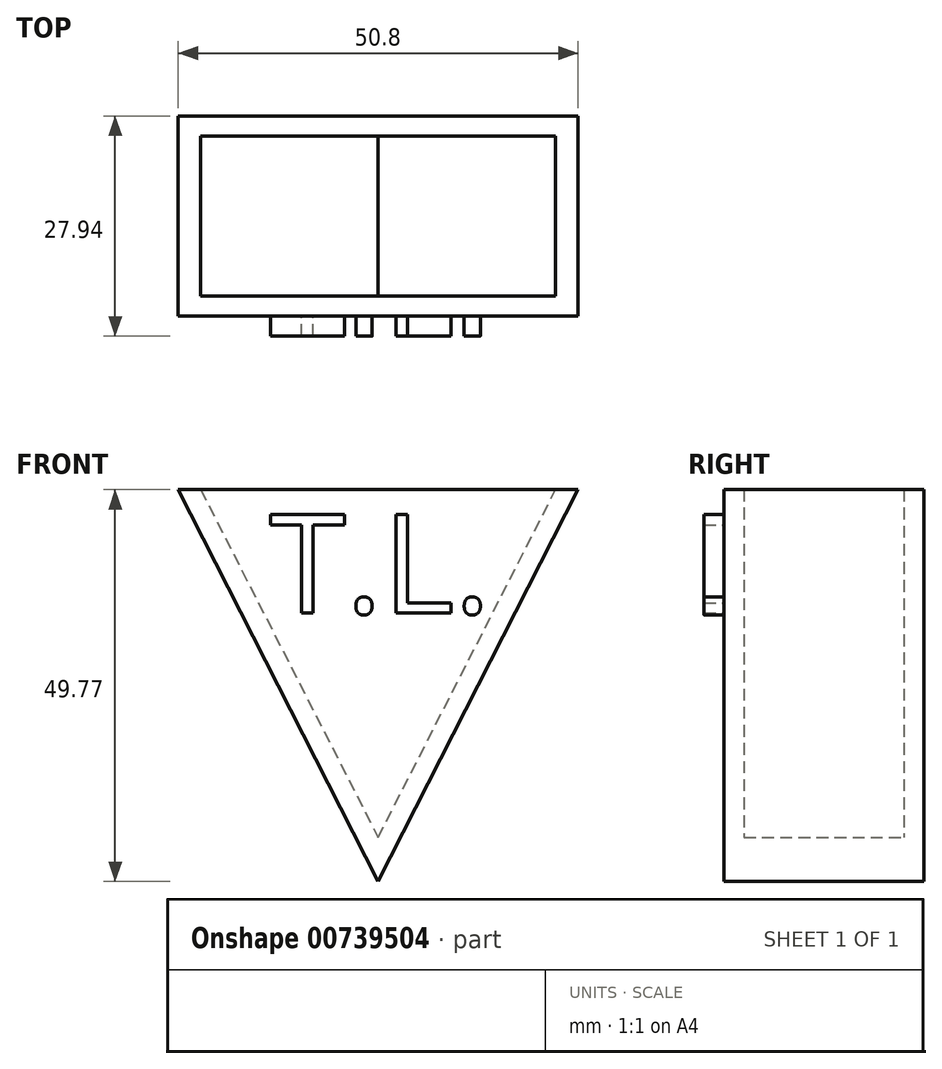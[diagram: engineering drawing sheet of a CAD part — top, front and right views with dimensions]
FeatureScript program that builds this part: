
annotation { "Feature Type Name" : "Feature", "Feature Type Description" : "" }
export const myFeature = defineFeature(function(context is Context, id is Id, definition is map)
    precondition{}
    {
        {
            var Q0;
            Q0=qCreatedBy(makeId("Front.planeOp"),FACE);
            var sketch = newSketch(context, id + "F0", { "sketchPlane" : qUnion([Q0])});
            skLineSegment(sketch, "E0", {"start": v(-25.4, 0) * mm, "end": v(0, -49.77) * mm});
            skLineSegment(sketch, "E1", {"start": v(0, -49.77) * mm, "end": v(25.4, 0) * mm});
            skLineSegment(sketch, "E2", {"start": v(0, 0) * mm, "end": v(25.4, 0) * mm});
            skLineSegment(sketch, "E3", {"start": v(0, 0) * mm, "end": v(-25.4, 0) * mm});
            skLineSegment(sketch, "E4", {"start": v(0, 0) * mm, "end": v(0, -50.8) * mm});
            skSolve(sketch);
        }
        {
            var Q0;
            {var subQ0=sQuery(id+"F0.wireOp",EDGE,"E1");Q0=makeQuery(id+"F0.imprint","IMPRINT",FACE,{"disambiguationData":[TD([[makeQuery(id+"F0.imprint","IMPRINT",EDGE,{"derivedFrom":subQ0}),1.0]])]});}
            var Q1;
            {var subQ0=sQuery(id+"F0.wireOp",EDGE,"E0");Q1=makeQuery(id+"F0.imprint","IMPRINT",FACE,{"disambiguationData":[TD([[makeQuery(id+"F0.imprint","IMPRINT",EDGE,{"derivedFrom":subQ0}),1.0]])]});}
            extrude(context, id + "F1", {"entities" : qUnion([Q0, Q1]), "depth" : 25.4 * mm, "offsetDistance" : 25.4 * mm});
        }
        {
            var Q0;
            Q0=makeQuery(id+"F1.opExtrude","SWEPT_FACE",FACE,{"disambiguationData":[OSD([sQuery(id+"F0.wireOp",EDGE,"E2"),sQuery(id+"F0.wireOp",EDGE,"E3")])]});
            shell(context, id + "F2", {"entities" : qUnion([Q0]), "thickness" : 2.54 * mm});
        }
        {
            var Q0;
            Q0=makeQuery(id+"F1.opExtrude","CAP_FACE",FACE,{"disambiguationData":[OSD([sQuery(id+"F0.wireOp",EDGE,"E0"),sQuery(id+"F0.wireOp",EDGE,"E1"),sQuery(id+"F0.wireOp",EDGE,"E2"),sQuery(id+"F0.wireOp",EDGE,"E3")])],"isStart":false});
            var sketch = newSketch(context, id + "F3", { "sketchPlane" : qUnion([Q0])});
            skText(sketch, "E5", { "text": "T.L.", "fontName": "OpenSans-Regular.ttf"});
            const initialGuessF3  = {"E5": [-0.01383, -0.0157, 1, 0, 0.01262]};
            skSetInitialGuess(sketch, initialGuessF3);
            skSolve(sketch);
        }
        {
            var Q0;
            Q0 = qSketchRegion(id + "F3", true);
            extrude(context, id + "F4", {"entities" : qUnion([Q0]), "operationType" : NewBodyOperationType.ADD, "depth" : 2.54 * mm, "offsetDistance" : 25.4 * mm});
        }
    });
